# Revit family: LHV4
name_source: partatom
category: Lighting Fixtures
revit_build: Autodesk Revit Architecture 2012 (Build: 20110309_2315(x64)
units: mm (PartAtom-declared; Revit-internal decimal feet)

## types (26) — shared parameters
Apparent Load = 0 VA
Backbox = White
Color Filter = 16777215
Default Elevation = 48.000"
Description = VersaBay® luminaires are the new industry standard for fluorescent high bay lighting with Advanced Thermal Management, serviceability, and performance that is unrivaled in the marketplace.
Dimming Lamp Color Temperature Shift = <None>
Emit from Line Length = 48.000"
Glass = Glass
Lamp = F54T5
Manufacturer = Columbia Lighting
Manufacturer Fax = 866-898-1065
Model = LHV4
Product Documentation Link = http://www.columbialighting.com
Product Page URL = http://www.columbialighting.com
Tilt Angle = -90.00°
URL = http://www.columbialighting.com
Wattage Comments = 235W

## per-type parameters (varying)
| type | Photometric Web File |
| LHV4-432-GWST | 14614 |
| LHV4-432-GWU | 14617 |
| LHV4-432-M4RST | 14621 |
| LHV4-432-M4RU | 14619 |
| LHV4-454-GWST | 14630 |
| LHV4-454-GWU | ITL58529 |
| LHV4-454-M4RST | 14634 |
| LHV4-454-M4RU | 14633 |
| LHV4-632-GWST | 14579 |
| LHV4-632-GWU | 14564 |
| LHV4-632-M4RST | 14578 |
| LHV4-632-M4RU | 14573 |
| LHV4-632-M4RU-CPWG | 15212 |
| LHV4-654-GWST | ITL58525 |
| LHV4-654-GWU | ITL58526 |
| LHV4-654-M4RST | ITL58527 |
| LHV4-654-M4RU | 14541 |
| LHV4-654-M4RU-CAWG | 15214 |
| LHV4-832-GW | 15127 |
| LHV4-832-GWU | 15191 |
| LHV4-832-M4R | 15126 |
| LHV4-832-M4RU | 15190 |
| LHV4-854-GW | 15181 |
| LHV4-854-GWU | 15189 |
| LHV4-854-M4RST | 15187 |
| LHV4-854-M4RU | 15188 |

## geometry (parser evidence)
native form markers: Sweep x1
no freeform markers — native parametric forms only
